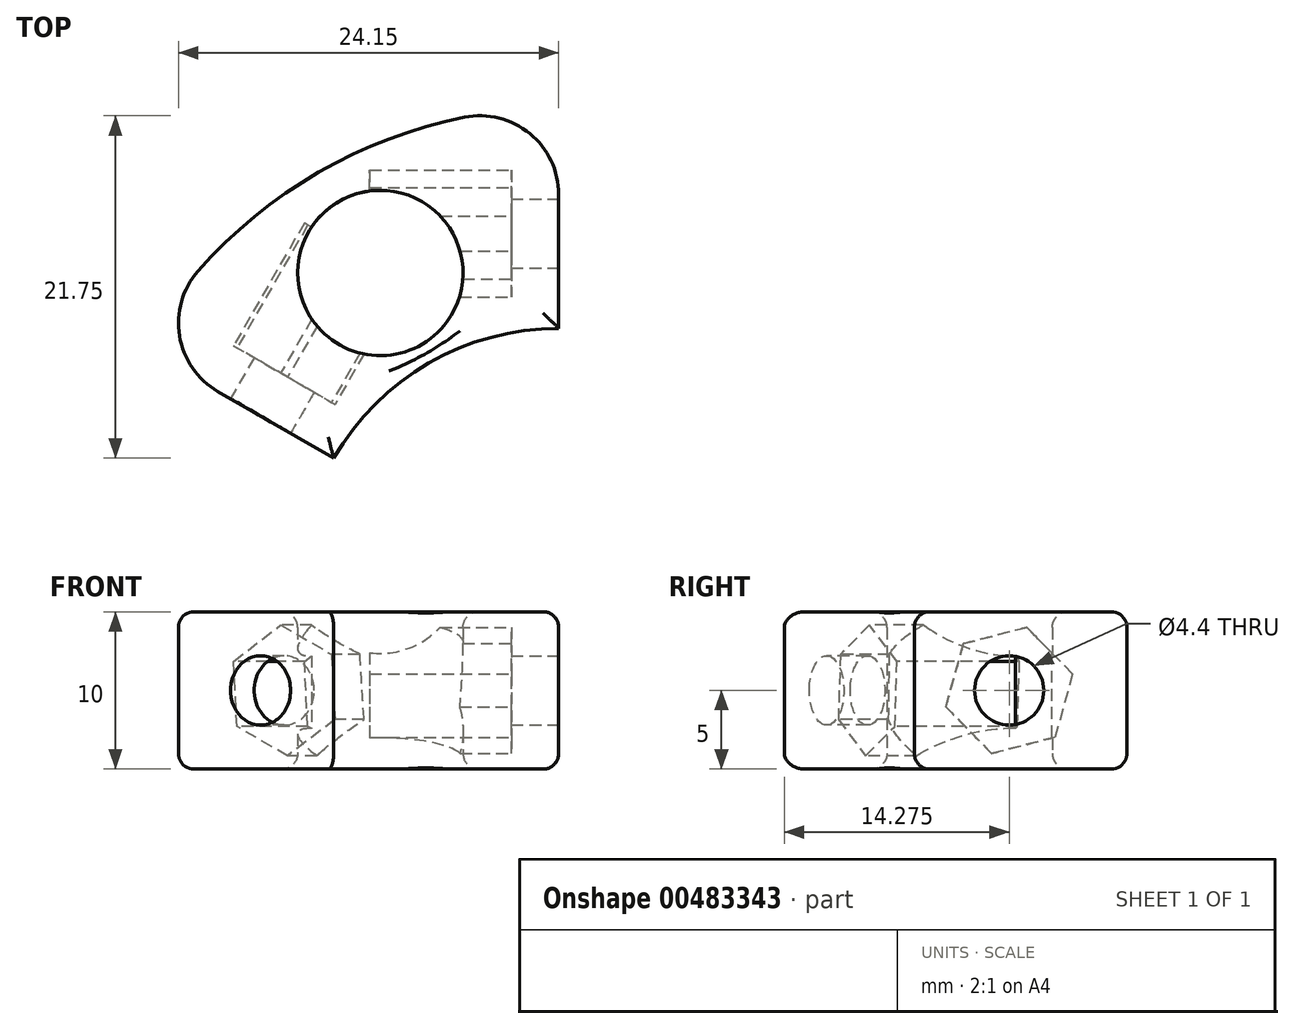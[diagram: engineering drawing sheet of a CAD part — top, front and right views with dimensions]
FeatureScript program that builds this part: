
annotation { "Feature Type Name" : "Feature", "Feature Type Description" : "" }
export const myFeature = defineFeature(function(context is Context, id is Id, definition is map)
    precondition{}
    {
        {
            var Q0;
            Q0=qCreatedBy(makeId("Top.planeOp"),FACE);
            var sketch = newSketch(context, id + "F0", { "sketchPlane" : qUnion([Q0])});
            skLineSegment(sketch, "E0", {"start": v(0, 18.5) * mm, "end": v(0, 18.5) * mm});
            skArc(sketch, "E1", {"start": v(-22.9, 20.13) * mm, "mid": v(-15.25, 26.41) * mm, "end": v(-5.98, 29.9) * mm});
            skLineSegment(sketch, "E2", {"start": v(0, 18.5) * mm, "end": v(0, 25) * mm});
            skLineSegment(sketch, "E3", {"start": v(0, 0) * mm, "end": v(-21.65, 12.5) * mm});
            skLineSegment(sketch, "E4", {"start": v(0, 18.5) * mm, "end": v(0, 24.5) * mm});
            skCircle(sketch, "E5", {"center": v(-11.33, 20.01) * mm, "radius": 5.25 * mm});
            skLineSegment(sketch, "E6", {"start": v(1, 18.47) * mm, "end": v(1, 18.47) * mm});
            skLineSegment(sketch, "E7", {"start": v(1, 18.47) * mm, "end": v(1, 25.97) * mm});
            skLineSegment(sketch, "E8", {"start": v(0, 16.5) * mm, "end": v(0, 18.5) * mm});
            skLineSegment(sketch, "E9", {"start": v(1, 18.47) * mm, "end": v(1, 16.47) * mm});
            skArc(sketch, "E10", {"start": v(0, 16.5) * mm, "mid": v(-8.25, 14.29) * mm, "end": v(-14.29, 8.25) * mm});
            skLineSegment(sketch, "E11", {"start": v(1.5, 26.47) * mm, "end": v(3.5, 26.47) * mm});
            skLineSegment(sketch, "E12", {"start": v(4, 25.97) * mm, "end": v(4, 19.08) * mm});
            skLineSegment(sketch, "E13", {"start": v(-14.7, 7.5) * mm, "end": v(-22.32, 11.9) * mm});
            skLineSegment(sketch, "E14", {"start": v(-23, 11.71) * mm, "end": v(-24, 9.98) * mm});
            skLineSegment(sketch, "E15", {"start": v(-23.82, 9.3) * mm, "end": v(-17.9, 5.88) * mm});
            skPoint(sketch, "E16.visualSharp", {"position": v(-26.41, 15.25) * mm});
            skArc(sketch, "E16.filletArc", {"start": v(-22.9, 20.13) * mm, "mid": v(-24.08, 16.02) * mm, "end": v(-21.65, 12.5) * mm});
            skPoint(sketch, "E17.visualSharp", {"position": v(0, 30.5) * mm});
            skArc(sketch, "E17.filletArc", {"start": v(0, 25) * mm, "mid": v(-1.83, 28.87) * mm, "end": v(-5.98, 29.9) * mm});
            skPoint(sketch, "E18.visualSharp", {"position": v(1, 26.47) * mm});
            skArc(sketch, "E18.filletArc", {"start": v(1.5, 26.47) * mm, "mid": v(1.15, 26.32) * mm, "end": v(1, 25.97) * mm});
            skPoint(sketch, "E19.visualSharp", {"position": v(4, 26.47) * mm});
            skArc(sketch, "E19.filletArc", {"start": v(4, 25.97) * mm, "mid": v(3.85, 26.32) * mm, "end": v(3.5, 26.47) * mm});
            skPoint(sketch, "E20.visualSharp", {"position": v(-24.26, 9.55) * mm});
            skArc(sketch, "E20.filletArc", {"start": v(-24, 9.98) * mm, "mid": v(-24.06, 9.6) * mm, "end": v(-23.82, 9.3) * mm});
            skPoint(sketch, "E21.visualSharp", {"position": v(-22.76, 12.14) * mm});
            skArc(sketch, "E21.filletArc", {"start": v(-22.32, 11.9) * mm, "mid": v(-22.7, 11.94) * mm, "end": v(-23, 11.71) * mm});
            skPoint(sketch, "E22.visualSharp", {"position": v(4, 18.25) * mm});
            skArc(sketch, "E22.filletArc", {"start": v(4, 19.08) * mm, "mid": v(4.22, 18.45) * mm, "end": v(4.8, 18.1) * mm});
            skLineSegment(sketch, "E23", {"start": v(8.9, -16.6) * mm, "end": v(7.7, -14.59) * mm});
            skLineSegment(sketch, "E24", {"start": v(5.85, -15.43) * mm, "end": v(6.49, -17.7) * mm});
            skArc(sketch, "E25", {"start": v(-17.9, 5.88) * mm, "mid": v(-13.1, -13.55) * mm, "end": v(6.49, -17.7) * mm});
            skArc(sketch, "E26.trimOffspring", {"start": v(8.9, -16.6) * mm, "mid": v(18.68, 2.45) * mm, "end": v(4.33, 18.34) * mm});
            skArc(sketch, "E27", {"start": v(1, 16.47) * mm, "mid": v(16.13, 3.48) * mm, "end": v(7.7, -14.59) * mm});
            skArc(sketch, "E28", {"start": v(5.85, -15.43) * mm, "mid": v(-12.29, -11.01) * mm, "end": v(-14.7, 7.5) * mm});
            skSolve(sketch);
        }
        {
            var Q0;
            Q0 = qSketchRegion(id + "F0", true);
            extrude(context, id + "F1", {"entities" : qUnion([Q0]), "depth" : 10 * mm});
        }
        {
            var Q0;
            Q0=makeQuery(id+"F1.opExtrude","SWEPT_FACE",FACE,{"disambiguationData":[OSD([sQuery(id+"F0.wireOp",EDGE,"E12")])]});
            var sketch = newSketch(context, id + "F2", { "sketchPlane" : qUnion([Q0])});
            skCircle(sketch, "E29", {"center": v(22.52, 5) * mm, "radius": 2.2 * mm});
            skPoint(sketch, "E29.centerSnap0", {"position": v(22.52, 0) * mm});
            skPoint(sketch, "E29.centerSnap1", {"position": v(19.08, 5) * mm});
            skSolve(sketch);
        }
        {
            var Q0;
            Q0 = qSketchRegion(id + "F2", true);
            extrude(context, id + "F3", {"entities" : qUnion([Q0]), "operationType" : NewBodyOperationType.REMOVE, "oppositeDirection" : true, "depth" : 8 * mm});
        }
        {
            var Q0;
            Q0=makeQuery(id+"F1.opExtrude","SWEPT_FACE",FACE,{"disambiguationData":[OSD([sQuery(id+"F0.wireOp",EDGE,"E15")])]});
            var sketch = newSketch(context, id + "F4", { "sketchPlane" : qUnion([Q0])});
            skCircle(sketch, "E30", {"center": v(-21.86, 5) * mm, "radius": 2.2 * mm});
            skPoint(sketch, "E30.centerSnap0", {"position": v(-21.86, 10) * mm});
            skPoint(sketch, "E30.centerSnap1", {"position": v(-25.28, 5) * mm});
            skSolve(sketch);
        }
        {
            var Q0;
            Q0=makeQuery(id+"F4.imprint","IMPRINT",FACE,{"disambiguationData":[TD([[makeQuery(id+"F4.imprint","IMPRINT",EDGE,{"derivedFrom":sQuery(id+"F4.wireOp",EDGE,"E30")}),1.0]])]});
            extrude(context, id + "F5", {"entities" : qUnion([Q0]), "operationType" : NewBodyOperationType.REMOVE, "oppositeDirection" : true, "depth" : 10 * mm});
        }
        {
            var Q0;
            Q0=makeQuery(id+"F1.opExtrude","SWEPT_FACE",FACE,{"disambiguationData":[OSD([sQuery(id+"F0.wireOp",EDGE,"E3")])]});
            var sketch = newSketch(context, id + "F6", { "sketchPlane" : qUnion([Q0])});
            skCircle(sketch, "E31.cCircle", {"center": v(-21.86, 5) * mm, "radius": 3.6 * mm, "construction": true});
            skLineSegment(sketch, "E31.0", {"start": v(-22.11, 9.15) * mm, "end": v(-18.4, 7.3) * mm});
            skLineSegment(sketch, "E31.1", {"start": v(-18.4, 7.3) * mm, "end": v(-18.14, 3.14) * mm});
            skLineSegment(sketch, "E31.2", {"start": v(-18.14, 3.14) * mm, "end": v(-21.6, 0.85) * mm});
            skLineSegment(sketch, "E31.3", {"start": v(-21.6, 0.85) * mm, "end": v(-25.33, 2.7) * mm});
            skLineSegment(sketch, "E31.4", {"start": v(-25.33, 2.7) * mm, "end": v(-25.58, 6.86) * mm});
            skLineSegment(sketch, "E31.5", {"start": v(-25.58, 6.86) * mm, "end": v(-22.11, 9.15) * mm});
            skPoint(sketch, "E31.0.midPoint", {"position": v(-20.25, 8.22) * mm});
            skSolve(sketch);
        }
        {
            var Q0;
            Q0=makeQuery(id+"F6.imprint","IMPRINT",FACE,{"disambiguationData":[TD([[makeQuery(id+"F6.imprint","IMPRINT",EDGE,{"derivedFrom":makeQuery(id+"F5.boolean.opBoolean","INTERSECT",EDGE,{"derivedFrom":[makeQuery(id+"F1.opExtrude","SWEPT_FACE",FACE,{"disambiguationData":[OSD([sQuery(id+"F0.wireOp",EDGE,"E3")])]}),makeQuery(id+"F5.opExtrude","SWEPT_FACE",FACE,{"disambiguationData":[OSD([sQuery(id+"F4.wireOp",EDGE,"E30")])]})]})}),1.0]])]});
            var Q1;
            {var subQ0=sQuery(id+"F6.wireOp",EDGE,"E31.4");Q1=makeQuery(id+"F6.imprint","IMPRINT",FACE,{"disambiguationData":[TD([[makeQuery(id+"F6.imprint","IMPRINT",EDGE,{"derivedFrom":subQ0}),-1.0]])]});}
            var Q2;
            {var subQ7=sQuery(id+"F6.wireOp",EDGE,"E31.0");Q2=makeQuery(id+"F6.imprint","IMPRINT",FACE,{"disambiguationData":[TD([[makeQuery(id+"F6.imprint","IMPRINT",EDGE,{"derivedFrom":subQ7}),-1.0]])]});}
            extrude(context, id + "F7", {"entities" : qUnion([Q0, Q1, Q2]), "operationType" : NewBodyOperationType.REMOVE, "oppositeDirection" : true, "depth" : 12 * mm, "hasSecondDirection" : true, "secondDirectionOppositeDirection" : true, "secondDirectionDepth" : 3 * mm});
        }
        {
            var Q0;
            Q0=makeQuery(id+"F1.opExtrude","SWEPT_FACE",FACE,{"disambiguationData":[OSD([sQuery(id+"F0.wireOp",EDGE,"E2"),sQuery(id+"F0.wireOp",EDGE,"E4"),sQuery(id+"F0.wireOp",EDGE,"E8")])]});
            var sketch = newSketch(context, id + "F8", { "sketchPlane" : qUnion([Q0])});
            skCircle(sketch, "E32.cCircle", {"center": v(22.52, 5) * mm, "radius": 3.6 * mm, "construction": true});
            skLineSegment(sketch, "E32.0", {"start": v(19.62, 7.97) * mm, "end": v(23.64, 9) * mm});
            skLineSegment(sketch, "E32.1", {"start": v(23.64, 9) * mm, "end": v(26.55, 6.03) * mm});
            skLineSegment(sketch, "E32.2", {"start": v(26.55, 6.03) * mm, "end": v(25.43, 2.03) * mm});
            skLineSegment(sketch, "E32.3", {"start": v(25.43, 2.03) * mm, "end": v(21.4, 1) * mm});
            skLineSegment(sketch, "E32.4", {"start": v(21.4, 1) * mm, "end": v(18.5, 3.97) * mm});
            skLineSegment(sketch, "E32.5", {"start": v(18.5, 3.97) * mm, "end": v(19.62, 7.97) * mm});
            skPoint(sketch, "E32.0.midPoint", {"position": v(21.63, 8.49) * mm});
            skSolve(sketch);
        }
        {
            var Q0;
            Q0 = qSketchRegion(id + "F8", true);
            extrude(context, id + "F9", {"entities" : qUnion([Q0]), "operationType" : NewBodyOperationType.REMOVE, "oppositeDirection" : true, "depth" : 12 * mm, "hasSecondDirection" : true, "secondDirectionOppositeDirection" : true, "secondDirectionDepth" : 3 * mm});
        }
        {
            var Q0;
            Q0=makeQuery(id+"F1.opExtrude","SWEPT_FACE",FACE,{"disambiguationData":[OSD([sQuery(id+"F0.wireOp",EDGE,"E24")])]});
            var Q1;
            Q1=makeQuery(id+"F1.opExtrude","SWEPT_FACE",FACE,{"disambiguationData":[OSD([sQuery(id+"F0.wireOp",EDGE,"E23")])]});
            var Q2;
            Q2=makeQuery(id+"F1.opExtrude","CAP_FACE",FACE,{"disambiguationData":[OSD([sQuery(id+"F0.wireOp",EDGE,"E13"),sQuery(id+"F0.wireOp",EDGE,"E14"),sQuery(id+"F0.wireOp",EDGE,"E15"),sQuery(id+"F0.wireOp",EDGE,"E20.filletArc"),sQuery(id+"F0.wireOp",EDGE,"E21.filletArc"),sQuery(id+"F0.wireOp",EDGE,"E24"),sQuery(id+"F0.wireOp",EDGE,"E25"),sQuery(id+"F0.wireOp",EDGE,"a188417b-cc8c-4509-bfe6-a5d54d56d6b7.trimOffspring")])],"isStart":false});
            var Q3;
            Q3=makeQuery(id+"F1.opExtrude","CAP_FACE",FACE,{"disambiguationData":[OSD([sQuery(id+"F0.wireOp",EDGE,"E7"),sQuery(id+"F0.wireOp",EDGE,"E9"),sQuery(id+"F0.wireOp",EDGE,"E11"),sQuery(id+"F0.wireOp",EDGE,"E12"),sQuery(id+"F0.wireOp",EDGE,"E18.filletArc"),sQuery(id+"F0.wireOp",EDGE,"E19.filletArc"),sQuery(id+"F0.wireOp",EDGE,"E22.filletArc"),sQuery(id+"F0.wireOp",EDGE,"E23"),sQuery(id+"F0.wireOp",EDGE,"jDdMIHg0-1Oi0-MaQn-ggq3-3935tTYizpBS"),sQuery(id+"F0.wireOp",EDGE,"E26.trimOffspring")])],"isStart":false});
            var Q4;
            Q4=makeQuery(id+"F1.opExtrude","CAP_FACE",FACE,{"disambiguationData":[OSD([sQuery(id+"F0.wireOp",EDGE,"E1"),sQuery(id+"F0.wireOp",EDGE,"E2"),sQuery(id+"F0.wireOp",EDGE,"E3"),sQuery(id+"F0.wireOp",EDGE,"E4"),sQuery(id+"F0.wireOp",EDGE,"E5"),sQuery(id+"F0.wireOp",EDGE,"E8"),sQuery(id+"F0.wireOp",EDGE,"E10"),sQuery(id+"F0.wireOp",EDGE,"E16.filletArc"),sQuery(id+"F0.wireOp",EDGE,"E17.filletArc")])],"isStart":false});
            var Q5;
            Q5=makeQuery(id+"F1.opExtrude","CAP_FACE",FACE,{"disambiguationData":[OSD([sQuery(id+"F0.wireOp",EDGE,"E1"),sQuery(id+"F0.wireOp",EDGE,"E2"),sQuery(id+"F0.wireOp",EDGE,"E3"),sQuery(id+"F0.wireOp",EDGE,"E4"),sQuery(id+"F0.wireOp",EDGE,"E5"),sQuery(id+"F0.wireOp",EDGE,"E8"),sQuery(id+"F0.wireOp",EDGE,"E10"),sQuery(id+"F0.wireOp",EDGE,"E16.filletArc"),sQuery(id+"F0.wireOp",EDGE,"E17.filletArc")])],"isStart":true});
            var Q6;
            Q6=makeQuery(id+"F1.opExtrude","CAP_FACE",FACE,{"disambiguationData":[OSD([sQuery(id+"F0.wireOp",EDGE,"E7"),sQuery(id+"F0.wireOp",EDGE,"E9"),sQuery(id+"F0.wireOp",EDGE,"E11"),sQuery(id+"F0.wireOp",EDGE,"E12"),sQuery(id+"F0.wireOp",EDGE,"E18.filletArc"),sQuery(id+"F0.wireOp",EDGE,"E19.filletArc"),sQuery(id+"F0.wireOp",EDGE,"E22.filletArc"),sQuery(id+"F0.wireOp",EDGE,"E23"),sQuery(id+"F0.wireOp",EDGE,"jDdMIHg0-1Oi0-MaQn-ggq3-3935tTYizpBS"),sQuery(id+"F0.wireOp",EDGE,"E26.trimOffspring")])],"isStart":true});
            var Q7;
            Q7=makeQuery(id+"F1.opExtrude","CAP_FACE",FACE,{"disambiguationData":[OSD([sQuery(id+"F0.wireOp",EDGE,"E13"),sQuery(id+"F0.wireOp",EDGE,"E14"),sQuery(id+"F0.wireOp",EDGE,"E15"),sQuery(id+"F0.wireOp",EDGE,"E20.filletArc"),sQuery(id+"F0.wireOp",EDGE,"E21.filletArc"),sQuery(id+"F0.wireOp",EDGE,"E24"),sQuery(id+"F0.wireOp",EDGE,"E25"),sQuery(id+"F0.wireOp",EDGE,"a188417b-cc8c-4509-bfe6-a5d54d56d6b7.trimOffspring")])],"isStart":true});
            fillet(context, id + "F10", {"entities" : qUnion([Q0, Q1, Q2, Q3, Q4, Q5, Q6, Q7]), "radius" : 1 * mm, "tangentPropagation" : true, "allowEdgeOverflow" : false});
        }
        {
            var Q0;
            Q0=makeQuery(id+"F1.opExtrude","SWEPT_BODY",BODY,{"disambiguationData":[OSD([sQuery(id+"F0.wireOp",EDGE,"E13"),sQuery(id+"F0.wireOp",EDGE,"E14"),sQuery(id+"F0.wireOp",EDGE,"E15"),sQuery(id+"F0.wireOp",EDGE,"E20.filletArc"),sQuery(id+"F0.wireOp",EDGE,"E21.filletArc"),sQuery(id+"F0.wireOp",EDGE,"E24"),sQuery(id+"F0.wireOp",EDGE,"E25"),sQuery(id+"F0.wireOp",EDGE,"E28")])]});
            var Q1;
            Q1=makeQuery(id+"F1.opExtrude","SWEPT_BODY",BODY,{"disambiguationData":[OSD([sQuery(id+"F0.wireOp",EDGE,"E7"),sQuery(id+"F0.wireOp",EDGE,"E9"),sQuery(id+"F0.wireOp",EDGE,"E11"),sQuery(id+"F0.wireOp",EDGE,"E12"),sQuery(id+"F0.wireOp",EDGE,"E18.filletArc"),sQuery(id+"F0.wireOp",EDGE,"E19.filletArc"),sQuery(id+"F0.wireOp",EDGE,"E22.filletArc"),sQuery(id+"F0.wireOp",EDGE,"E23"),sQuery(id+"F0.wireOp",EDGE,"E26.trimOffspring"),sQuery(id+"F0.wireOp",EDGE,"E27")])]});
            deleteBodies(context, id + "F11", {"entities" : qUnion([Q0, Q1])});
        }
    });
